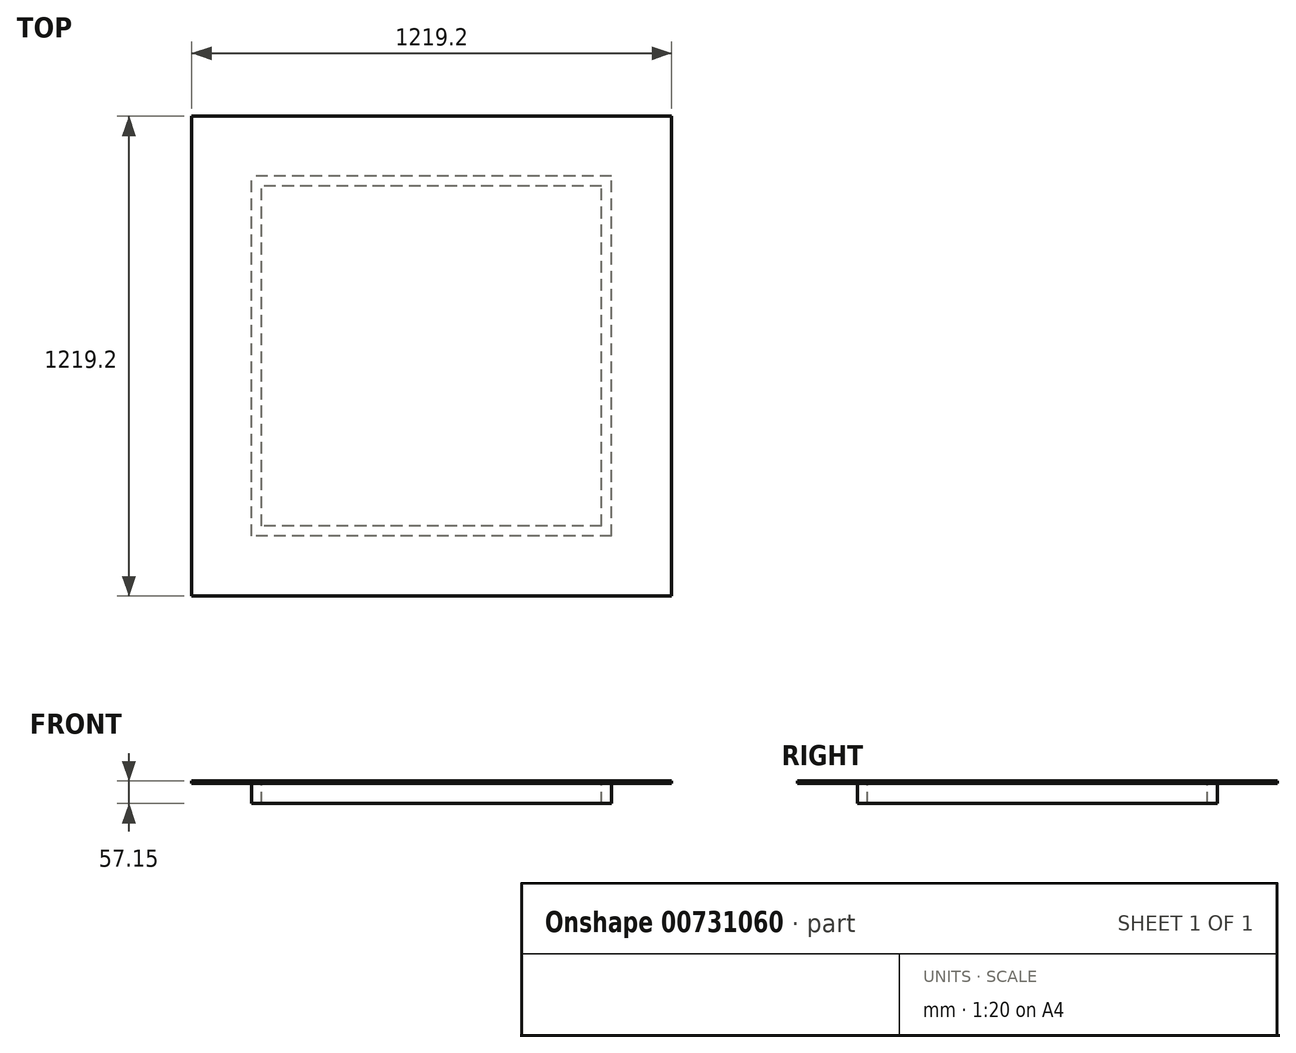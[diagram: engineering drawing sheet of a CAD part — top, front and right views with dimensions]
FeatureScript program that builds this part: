
annotation { "Feature Type Name" : "Feature", "Feature Type Description" : "" }
export const myFeature = defineFeature(function(context is Context, id is Id, definition is map)
    precondition{}
    {
        {
            var Q0;
            Q0=qCreatedBy(makeId("Top.planeOp"),FACE);
            var sketch = newSketch(context, id + "F0", { "sketchPlane" : qUnion([Q0])});
            skLineSegment(sketch, "E0.bottom", {"start": v(609.6, -609.6) * mm, "end": v(-609.6, -609.6) * mm});
            skLineSegment(sketch, "E0.top", {"start": v(609.6, 609.6) * mm, "end": v(-609.6, 609.6) * mm});
            skLineSegment(sketch, "E0.left", {"start": v(609.6, -609.6) * mm, "end": v(609.6, 609.6) * mm});
            skLineSegment(sketch, "E0.right", {"start": v(-609.6, -609.6) * mm, "end": v(-609.6, 609.6) * mm});
            skPoint(sketch, "E0.middle", {"position": v(0, 0) * mm});
            skLineSegment(sketch, "E1.bottom", {"start": v(457.2, -457.2) * mm, "end": v(-457.2, -457.2) * mm});
            skLineSegment(sketch, "E1.top", {"start": v(457.2, 457.2) * mm, "end": v(-457.2, 457.2) * mm});
            skLineSegment(sketch, "E1.left", {"start": v(457.2, -457.2) * mm, "end": v(457.2, 457.2) * mm});
            skLineSegment(sketch, "E1.right", {"start": v(-457.2, -457.2) * mm, "end": v(-457.2, 457.2) * mm});
            skSolve(sketch);
        }
        {
            var Q0;
            Q0=makeQuery(id+"F0.imprint","IMPRINT",FACE,{"disambiguationData":[TD([[makeQuery(id+"F0.imprint","IMPRINT",EDGE,{"derivedFrom":sQuery(id+"F0.wireOp",EDGE,"E1.bottom")}),-1.0]])]});
            var Q1;
            Q1=makeQuery(id+"F0.imprint","IMPRINT",FACE,{"disambiguationData":[TD([[makeQuery(id+"F0.imprint","IMPRINT",EDGE,{"derivedFrom":sQuery(id+"F0.wireOp",EDGE,"E0.bottom")}),-1.0]])]});
            extrude(context, id + "F1", {"entities" : qUnion([Q0, Q1]), "depth" : 6.35 * mm, "offsetDistance" : 25.4 * mm});
        }
        {
            var Q0;
            Q0=makeQuery(id+"F1.opExtrude","CAP_FACE",FACE,{"disambiguationData":[OSD([sQuery(id+"F0.wireOp",EDGE,"E0.bottom"),sQuery(id+"F0.wireOp",EDGE,"E0.top"),sQuery(id+"F0.wireOp",EDGE,"E0.left"),sQuery(id+"F0.wireOp",EDGE,"E0.right")])],"isStart":false});
            var sketch = newSketch(context, id + "F2", { "sketchPlane" : qUnion([Q0])});
            skLineSegment(sketch, "E2.bottom", {"start": v(457.2, -457.2) * mm, "end": v(-457.2, -457.2) * mm});
            skLineSegment(sketch, "E2.top", {"start": v(457.2, 457.2) * mm, "end": v(-457.2, 457.2) * mm});
            skLineSegment(sketch, "E2.left", {"start": v(457.2, -457.2) * mm, "end": v(457.2, 457.2) * mm});
            skLineSegment(sketch, "E2.right", {"start": v(-457.2, -457.2) * mm, "end": v(-457.2, 457.2) * mm});
            skPoint(sketch, "E2.middle", {"position": v(0, 0) * mm});
            skLineSegment(sketch, "E3.bottom", {"start": v(431.8, -431.8) * mm, "end": v(-431.8, -431.8) * mm});
            skLineSegment(sketch, "E3.top", {"start": v(431.8, 431.8) * mm, "end": v(-431.8, 431.8) * mm});
            skLineSegment(sketch, "E3.left", {"start": v(431.8, -431.8) * mm, "end": v(431.8, 431.8) * mm});
            skLineSegment(sketch, "E3.right", {"start": v(-431.8, -431.8) * mm, "end": v(-431.8, 431.8) * mm});
            skSolve(sketch);
        }
        {
            var Q0;
            Q0=makeQuery(id+"F2.imprint","IMPRINT",FACE,{"disambiguationData":[TD([[makeQuery(id+"F2.imprint","IMPRINT",EDGE,{"derivedFrom":sQuery(id+"F2.wireOp",EDGE,"E2.bottom")}),-1.0]])]});
            extrude(context, id + "F3", {"entities" : qUnion([Q0]), "operationType" : NewBodyOperationType.ADD, "oppositeDirection" : true, "depth" : 57.15 * mm, "offsetDistance" : 25.4 * mm});
        }
    });
